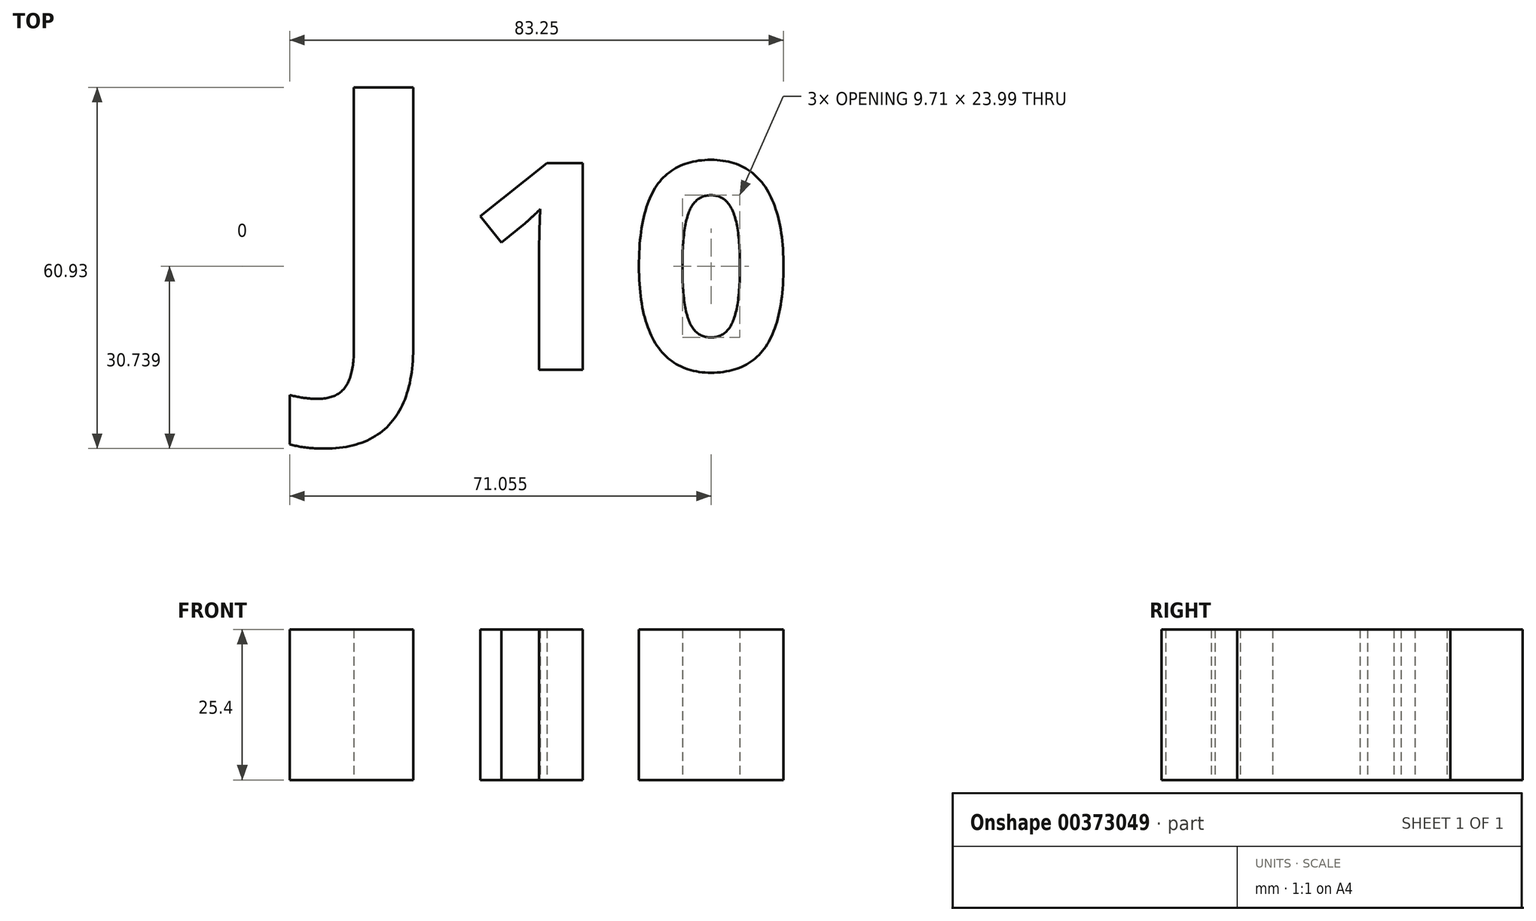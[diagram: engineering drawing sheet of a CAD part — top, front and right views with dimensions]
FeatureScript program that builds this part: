
annotation { "Feature Type Name" : "Feature", "Feature Type Description" : "" }
export const myFeature = defineFeature(function(context is Context, id is Id, definition is map)
    precondition{}
    {
        {
            var Q0;
            Q0=qCreatedBy(makeId("Top.planeOp"),FACE);
            var sketch = newSketch(context, id + "F0", { "sketchPlane" : qUnion([Q0])});
            skText(sketch, "E0", { "text": "J", "fontName": "OpenSans-Bold.ttf"});
            skText(sketch, "E1", { "text": "10", "fontName": "OpenSans-Bold.ttf"});
            const initialGuessF0  = {"E0": [-0.04928, 0.01457, 1, 0, 0.04748], "E1": [-0.02494, 0.014, 1, 0, 0.03517]};
            skSetInitialGuess(sketch, initialGuessF0);
            skSolve(sketch);
        }
        {
            var Q0;
            Q0 = qSketchRegion(id + "F0", true);
            extrude(context, id + "F1", {"entities" : qUnion([Q0]), "depth" : 25.4 * mm});
        }
        {
            var Q0;
            Q0 = qSketchRegion(id + "F0", true);
            extrude(context, id + "F2", {"entities" : qUnion([Q0]), "depth" : 25.4 * mm});
        }
        {
            var Q0;
            Q0 = qSketchRegion(id + "F0", true);
            extrude(context, id + "F3", {"entities" : qUnion([Q0]), "depth" : 25.4 * mm});
        }
    });
